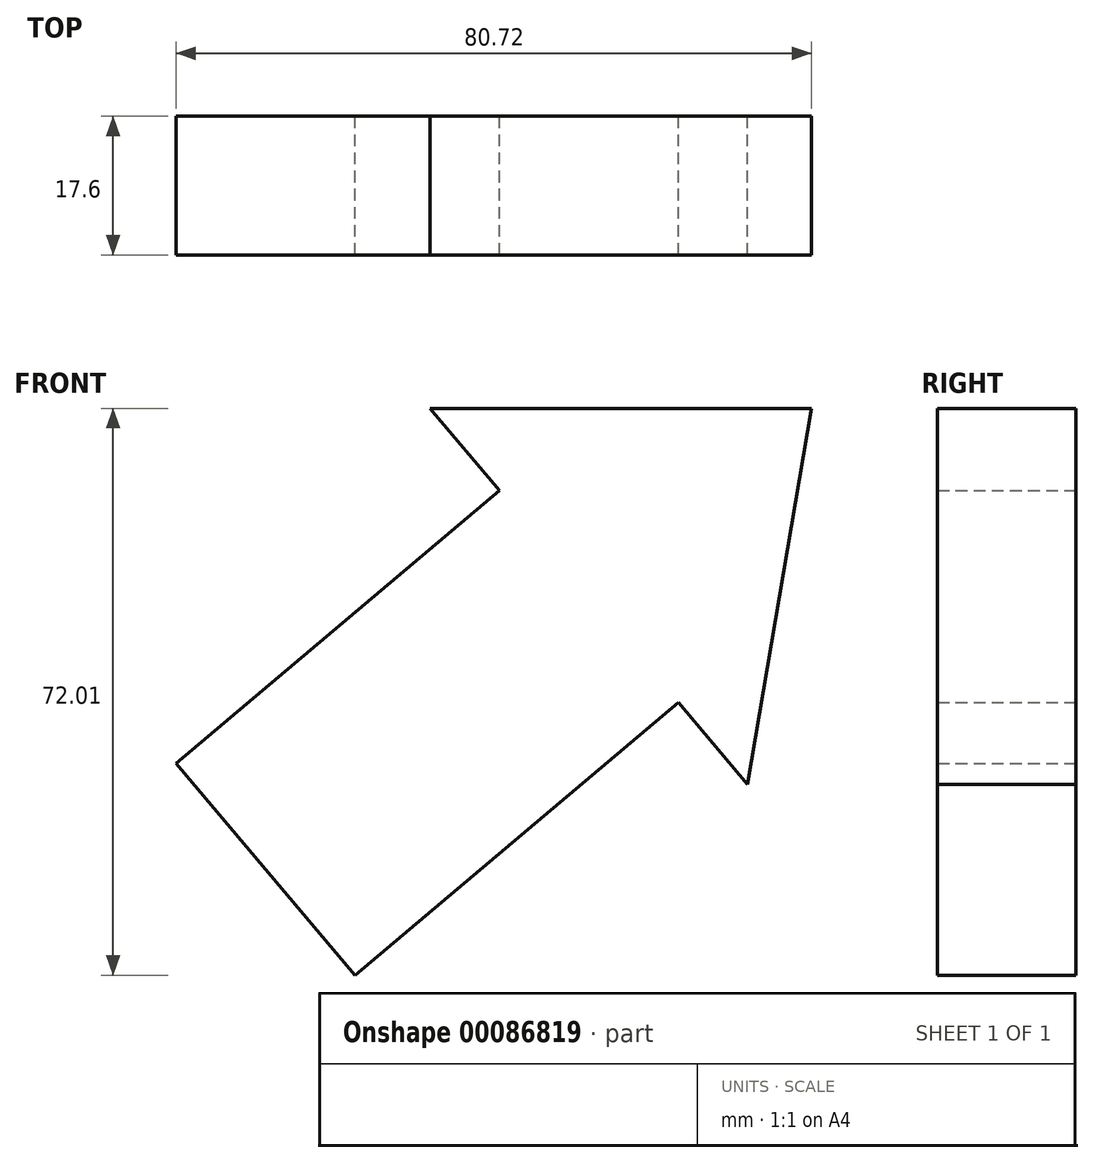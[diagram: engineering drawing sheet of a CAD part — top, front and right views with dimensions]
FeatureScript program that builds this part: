
annotation { "Feature Type Name" : "Feature", "Feature Type Description" : "" }
export const myFeature = defineFeature(function(context is Context, id is Id, definition is map)
    precondition{}
    {
        {
            var Q0;
            Q0=qCreatedBy(makeId("Front.planeOp"),FACE);
            var sketch = newSketch(context, id + "F0", { "sketchPlane" : qUnion([Q0])});
            skLineSegment(sketch, "E0", {"start": v(0, 0) * mm, "end": v(41.06, 34.67) * mm});
            skLineSegment(sketch, "E1", {"start": v(41.06, 34.67) * mm, "end": v(32.27, 45.08) * mm});
            skLineSegment(sketch, "E2", {"start": v(32.27, 45.08) * mm, "end": v(80.72, 45.08) * mm});
            skLineSegment(sketch, "E3", {"start": v(0, -23.06) * mm, "end": v(74.88, 40.15) * mm, "construction": true});
            skLineSegment(sketch, "E4.MirrorCS", {"start": v(22.73, -26.93) * mm, "end": v(63.8, 7.74) * mm});
            skLineSegment(sketch, "E5.MirrorCS", {"start": v(63.8, 7.74) * mm, "end": v(72.6, -2.68) * mm});
            skLineSegment(sketch, "E6.MirrorCS", {"start": v(72.6, -2.68) * mm, "end": v(80.72, 45.08) * mm});
            skLineSegment(sketch, "E7", {"start": v(0, 0) * mm, "end": v(22.73, -26.93) * mm});
            skSolve(sketch);
        }
        {
            var Q0;
            Q0=makeQuery(id+"F0.imprint","IMPRINT",FACE,{"disambiguationData":[TD([[makeQuery(id+"F0.imprint","IMPRINT",EDGE,{"derivedFrom":sQuery(id+"F0.wireOp",EDGE,"E0")}),-1.0]])]});
            extrude(context, id + "F1", {"entities" : qUnion([Q0]), "depth" : 17.6 * mm});
        }
    });
